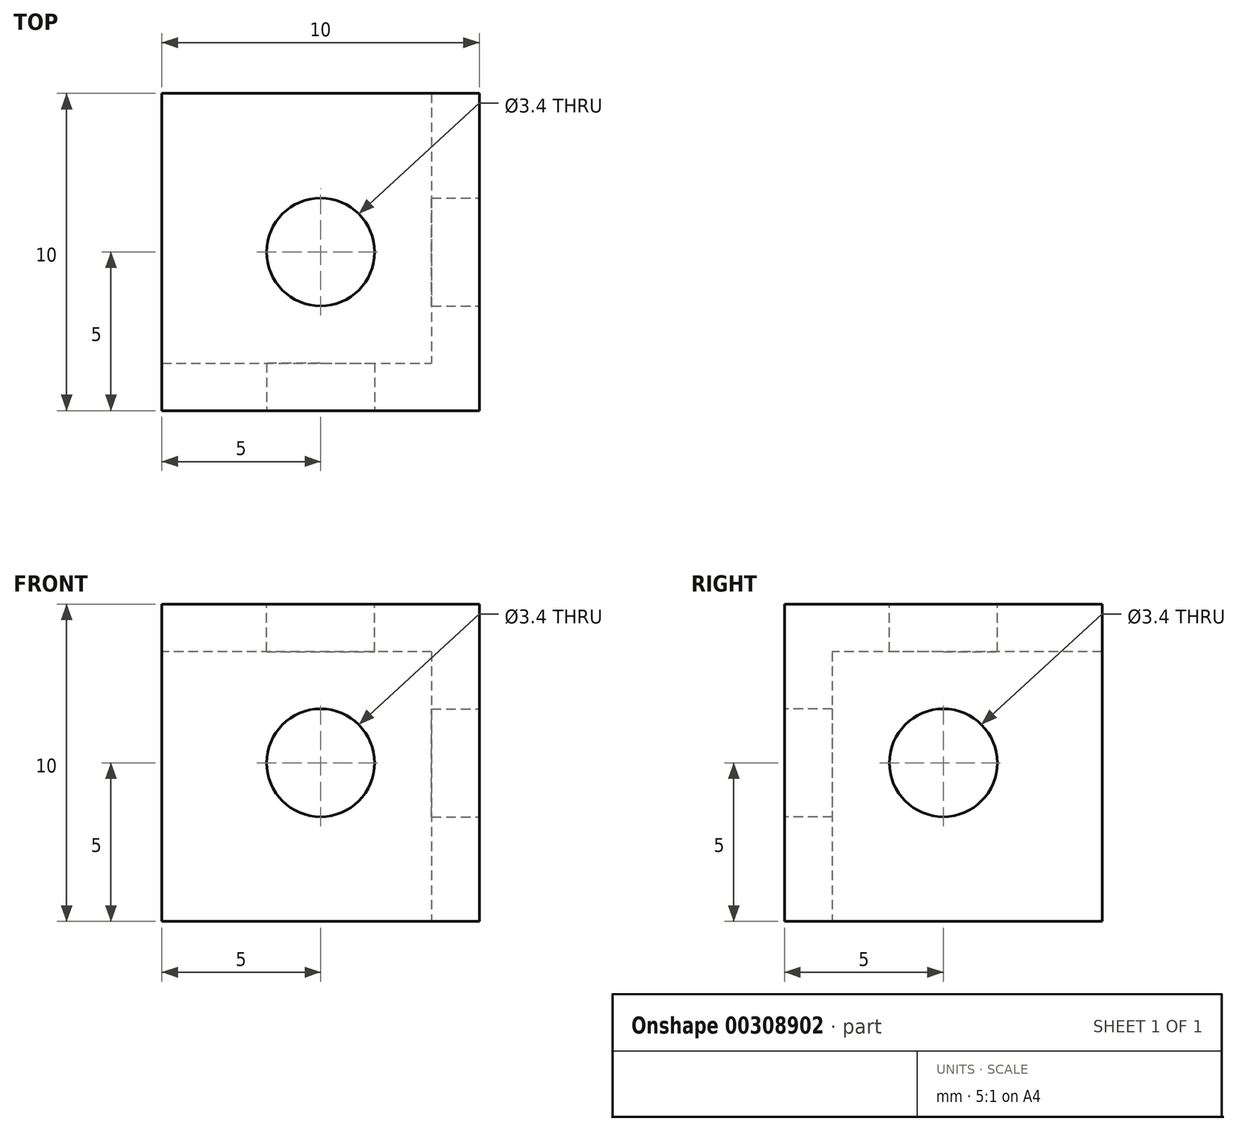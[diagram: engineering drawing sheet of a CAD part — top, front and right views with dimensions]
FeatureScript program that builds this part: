
annotation { "Feature Type Name" : "Feature", "Feature Type Description" : "" }
export const myFeature = defineFeature(function(context is Context, id is Id, definition is map)
    precondition{}
    {
        {
            var Q0;
            Q0=qCreatedBy(makeId("Top.planeOp"),FACE);
            var sketch = newSketch(context, id + "F0", { "sketchPlane" : qUnion([Q0])});
            skLineSegment(sketch, "E0.bottom", {"start": v(5, 5) * mm, "end": v(-5, 5) * mm});
            skLineSegment(sketch, "E0.top", {"start": v(5, -5) * mm, "end": v(-5, -5) * mm});
            skLineSegment(sketch, "E0.left", {"start": v(5, 5) * mm, "end": v(5, -5) * mm});
            skLineSegment(sketch, "E0.right", {"start": v(-5, 5) * mm, "end": v(-5, -5) * mm});
            skPoint(sketch, "E0.middle", {"position": v(0, 0) * mm});
            skSolve(sketch);
        }
        {
            var Q0;
            Q0=makeQuery(id+"F0.imprint","IMPRINT",FACE,{"disambiguationData":[TD([[makeQuery(id+"F0.imprint","IMPRINT",EDGE,{"derivedFrom":sQuery(id+"F0.wireOp",EDGE,"E0.bottom")}),1.0]])]});
            extrude(context, id + "F1", {"entities" : qUnion([Q0]), "depth" : 10 * mm});
        }
        {
            var Q0;
            Q0=makeQuery(id+"F1.opExtrude","CAP_FACE",FACE,{"disambiguationData":[OSD([sQuery(id+"F0.wireOp",EDGE,"E0.bottom"),sQuery(id+"F0.wireOp",EDGE,"E0.top"),sQuery(id+"F0.wireOp",EDGE,"E0.left"),sQuery(id+"F0.wireOp",EDGE,"E0.right")])],"isStart":true});
            var sketch = newSketch(context, id + "F2", { "sketchPlane" : qUnion([Q0])});
            skLineSegment(sketch, "E1.bottom", {"start": v(-5, -5) * mm, "end": v(3.5, -5) * mm});
            skLineSegment(sketch, "E1.top", {"start": v(-5, 3.5) * mm, "end": v(3.5, 3.5) * mm});
            skLineSegment(sketch, "E1.left", {"start": v(-5, -5) * mm, "end": v(-5, 3.5) * mm});
            skLineSegment(sketch, "E1.right", {"start": v(3.5, -5) * mm, "end": v(3.5, 3.5) * mm});
            skSolve(sketch);
        }
        {
            var Q0;
            Q0=makeQuery(id+"F2.imprint","IMPRINT",FACE,{"disambiguationData":[TD([[makeQuery(id+"F2.imprint","IMPRINT",EDGE,{"derivedFrom":sQuery(id+"F2.wireOp",EDGE,"E1.bottom")}),-1.0]])]});
            extrude(context, id + "F3", {"entities" : qUnion([Q0]), "operationType" : NewBodyOperationType.REMOVE, "oppositeDirection" : true, "depth" : 8.5 * mm});
        }
        {
            var Q0;
            Q0=makeQuery(id+"F1.opExtrude","SWEPT_FACE",FACE,{"disambiguationData":[OSD([sQuery(id+"F0.wireOp",EDGE,"E0.left")])]});
            var sketch = newSketch(context, id + "F4", { "sketchPlane" : qUnion([Q0])});
            skCircle(sketch, "E2", {"center": v(0, 5) * mm, "radius": 1.7 * mm});
            skPoint(sketch, "E2.centerSnap0", {"position": v(5, 5) * mm});
            skSolve(sketch);
        }
        {
            var Q0;
            Q0=makeQuery(id+"F4.imprint","IMPRINT",FACE,{"disambiguationData":[TD([[makeQuery(id+"F4.imprint","IMPRINT",EDGE,{"derivedFrom":sQuery(id+"F4.wireOp",EDGE,"E2")}),1.0]])]});
            extrude(context, id + "F5", {"entities" : qUnion([Q0]), "operationType" : NewBodyOperationType.REMOVE, "oppositeDirection" : true, "depth" : 25 * mm});
        }
        {
            var Q0;
            Q0=makeQuery(id+"F1.opExtrude","CAP_FACE",FACE,{"disambiguationData":[OSD([sQuery(id+"F0.wireOp",EDGE,"E0.bottom"),sQuery(id+"F0.wireOp",EDGE,"E0.top"),sQuery(id+"F0.wireOp",EDGE,"E0.left"),sQuery(id+"F0.wireOp",EDGE,"E0.right")])],"isStart":false});
            var sketch = newSketch(context, id + "F6", { "sketchPlane" : qUnion([Q0])});
            skCircle(sketch, "E3", {"center": v(0, 0) * mm, "radius": 1.7 * mm});
            skSolve(sketch);
        }
        {
            var Q0;
            Q0=makeQuery(id+"F6.imprint","IMPRINT",FACE,{"disambiguationData":[TD([[makeQuery(id+"F6.imprint","IMPRINT",EDGE,{"derivedFrom":sQuery(id+"F6.wireOp",EDGE,"E3")}),1.0]])]});
            extrude(context, id + "F7", {"entities" : qUnion([Q0]), "operationType" : NewBodyOperationType.REMOVE, "oppositeDirection" : true, "depth" : 25 * mm});
        }
        {
            var Q0;
            Q0=makeQuery(id+"F1.opExtrude","SWEPT_FACE",FACE,{"disambiguationData":[OSD([sQuery(id+"F0.wireOp",EDGE,"E0.top")])]});
            var sketch = newSketch(context, id + "F8", { "sketchPlane" : qUnion([Q0])});
            skCircle(sketch, "E4", {"center": v(0, 5) * mm, "radius": 1.7 * mm});
            skPoint(sketch, "E4.centerSnap0", {"position": v(5, 5) * mm});
            skPoint(sketch, "E4.centerSnap1", {"position": v(0, 10) * mm});
            skSolve(sketch);
        }
        {
            var Q0;
            Q0=makeQuery(id+"F8.imprint","IMPRINT",FACE,{"disambiguationData":[TD([[makeQuery(id+"F8.imprint","IMPRINT",EDGE,{"derivedFrom":sQuery(id+"F8.wireOp",EDGE,"E4")}),1.0]])]});
            extrude(context, id + "F9", {"entities" : qUnion([Q0]), "operationType" : NewBodyOperationType.REMOVE, "oppositeDirection" : true, "depth" : 25 * mm});
        }
    });
